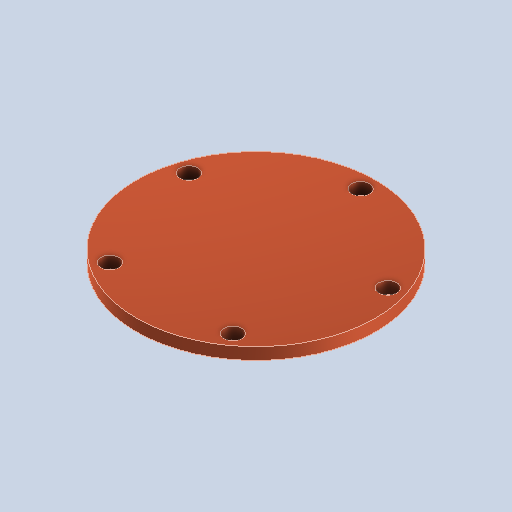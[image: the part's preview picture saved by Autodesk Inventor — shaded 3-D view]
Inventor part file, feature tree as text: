
AUTODESK INVENTOR PART (.ipt)
format: ipt  version: 2025.1 (Build 291241000, 241)  size: 244,224 bytes
history: native  units: mm
features: sketch x2, extrude x1, hole x1, pattern_circular x1
ambient origin geometry x8: Origin, YZ Plane, XZ Plane, XY Plane, X Axis, Y Axis, Z Axis, Center Point
bodies: Solid1 (feature_tree)
feature tree (5):
  extrude  "Extrusion1"  Depth=2.0mm TaperAngle=0.0deg
  hole  "Hole1"  [1 undecoded]
  pattern_circular  "Circular Pattern1"  [2 undecoded]
  sketch  "Sketch1"  dims[d0=40.0mm d1=2.0mm d2=0.0mm]
  sketch  "Sketch2"  dims[d3=35.0mm d4=3.0mm d5=6.0mm d6=4.0mm d7=2.0mm d8=90.0deg d9=8.0mm d10=0.0mm d11=50.0mm d12=360.0deg]
note: 3 required parameter values undecoded (feature->parameter linkage not recoverable at this tier; creation-order binding heuristic only, values carry confidence <= 0.55)
